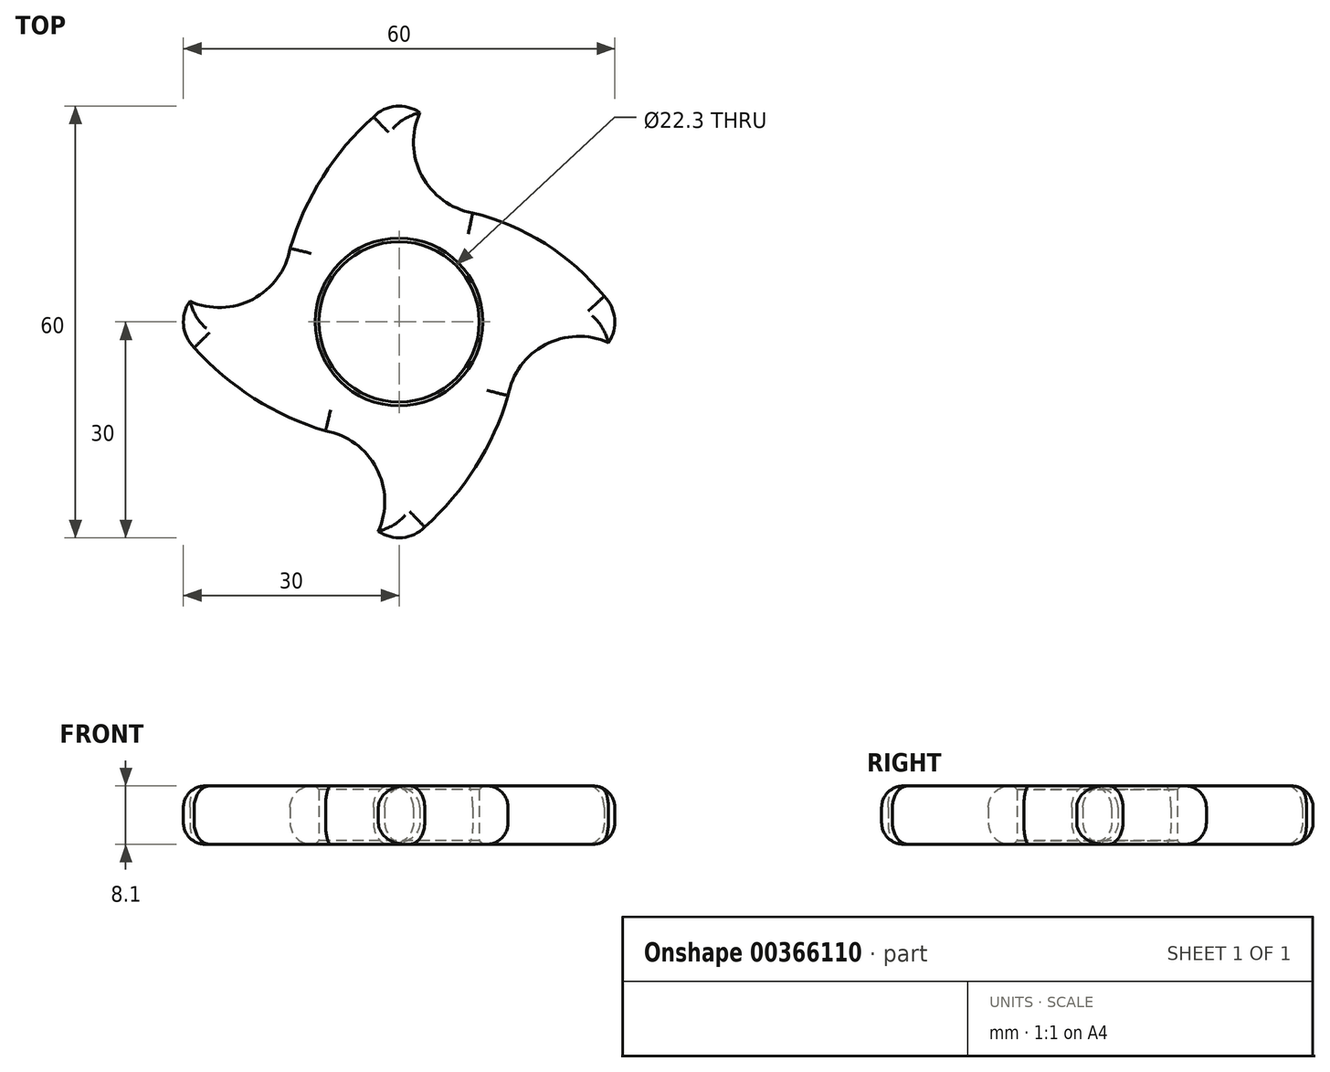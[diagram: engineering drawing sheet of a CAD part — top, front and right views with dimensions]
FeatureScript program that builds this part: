
annotation { "Feature Type Name" : "Feature", "Feature Type Description" : "" }
export const myFeature = defineFeature(function(context is Context, id is Id, definition is map)
    precondition{}
    {
        {
            var Q0;
            Q0=qCreatedBy(makeId("Top.planeOp"),FACE);
            var sketch = newSketch(context, id + "F0", { "sketchPlane" : qUnion([Q0])});
            skCircle(sketch, "E0", {"center": v(0, 0) * mm, "radius": 11.15 * mm});
            skArc(sketch, "E1", {"start": v(29.1, -2.88) * mm, "mid": v(29.98, 0.45) * mm, "end": v(28.51, 3.56) * mm});
            skArc(sketch, "E2", {"start": v(28.51, 3.56) * mm, "mid": v(20.33, 10.86) * mm, "end": v(10.23, 15.16) * mm});
            skArc(sketch, "E3.MirrorCS", {"start": v(-28.51, -3.56) * mm, "mid": v(-29.98, -0.45) * mm, "end": v(-29.1, 2.87) * mm});
            skArc(sketch, "E4.MirrorCS", {"start": v(-28.51, -3.56) * mm, "mid": v(-20.17, -10.62) * mm, "end": v(-10.23, -15.16) * mm});
            skArc(sketch, "E5", {"start": v(-29.1, 2.87) * mm, "mid": v(-20.33, 3.16) * mm, "end": v(-15.16, 10.23) * mm});
            skPoint(sketch, "E6.orphan", {"position": v(-28.51, 3.56) * mm});
            skPoint(sketch, "E7.visualSharp", {"position": v(-15.04, 12.9) * mm});
            skArc(sketch, "E8.MirrorCS", {"start": v(29.1, -2.87) * mm, "mid": v(20.33, -3.16) * mm, "end": v(15.16, -10.23) * mm});
            skPoint(sketch, "E9.orphan", {"position": v(28.51, -3.56) * mm});
            skArc(sketch, "E10.MirrorCS", {"start": v(-2.87, -29.1) * mm, "mid": v(-3.16, -20.33) * mm, "end": v(-10.23, -15.16) * mm});
            skArc(sketch, "E11.MirrorCS", {"start": v(3.56, -28.51) * mm, "mid": v(0.45, -29.98) * mm, "end": v(-2.88, -29.1) * mm});
            skArc(sketch, "E12.MirrorCS", {"start": v(3.56, -28.51) * mm, "mid": v(10.62, -20.17) * mm, "end": v(15.16, -10.23) * mm});
            skArc(sketch, "E13.MirrorCS", {"start": v(-3.56, 28.51) * mm, "mid": v(-10.62, 20.17) * mm, "end": v(-15.16, 10.23) * mm});
            skArc(sketch, "E14.MirrorCS", {"start": v(-3.56, 28.51) * mm, "mid": v(-0.45, 29.98) * mm, "end": v(2.88, 29.1) * mm});
            skArc(sketch, "E15.MirrorCS", {"start": v(2.87, 29.1) * mm, "mid": v(3.16, 20.33) * mm, "end": v(10.23, 15.16) * mm});
            skPoint(sketch, "E16.orphan", {"position": v(0, 16.05) * mm});
            skSolve(sketch);
        }
        {
            var Q0;
            Q0 = qSketchRegion(id + "F0", true);
            extrude(context, id + "F1", {"entities" : qUnion([Q0]), "depth" : 8.1 * mm});
        }
        {
            var Q0;
            Q0=makeQuery(id+"F1.opExtrude","CAP_EDGE",EDGE,{"disambiguationData":[OSD([sQuery(id+"F0.wireOp",EDGE,"E0")])],"isStart":false});
            var Q1;
            Q1=makeQuery(id+"F1.opExtrude","CAP_EDGE",EDGE,{"disambiguationData":[OSD([sQuery(id+"F0.wireOp",EDGE,"E0")])],"isStart":true});
            chamfer(context, id + "F2", {"entities" : qUnion([Q0, Q1]), "width" : .5 * mm, "tangentPropagation" : true});
        }
        {
            var Q0;
            Q0=makeQuery(id+"F1.opExtrude","CAP_EDGE",EDGE,{"disambiguationData":[OSD([sQuery(id+"F0.wireOp",EDGE,"E5")])],"isStart":false});
            var Q1;
            Q1=makeQuery(id+"F1.opExtrude","CAP_EDGE",EDGE,{"disambiguationData":[OSD([sQuery(id+"F0.wireOp",EDGE,"E13.MirrorCS")])],"isStart":false});
            var Q2;
            Q2=makeQuery(id+"F1.opExtrude","CAP_EDGE",EDGE,{"disambiguationData":[OSD([sQuery(id+"F0.wireOp",EDGE,"E14.MirrorCS")])],"isStart":false});
            var Q3;
            Q3=makeQuery(id+"F1.opExtrude","CAP_EDGE",EDGE,{"disambiguationData":[OSD([sQuery(id+"F0.wireOp",EDGE,"E15.MirrorCS")])],"isStart":false});
            var Q4;
            Q4=makeQuery(id+"F1.opExtrude","CAP_EDGE",EDGE,{"disambiguationData":[OSD([sQuery(id+"F0.wireOp",EDGE,"E2")])],"isStart":false});
            var Q5;
            Q5=makeQuery(id+"F1.opExtrude","CAP_EDGE",EDGE,{"disambiguationData":[OSD([sQuery(id+"F0.wireOp",EDGE,"E1")])],"isStart":false});
            var Q6;
            Q6=makeQuery(id+"F1.opExtrude","CAP_EDGE",EDGE,{"disambiguationData":[OSD([sQuery(id+"F0.wireOp",EDGE,"E8.MirrorCS")])],"isStart":false});
            var Q7;
            Q7=makeQuery(id+"F1.opExtrude","CAP_EDGE",EDGE,{"disambiguationData":[OSD([sQuery(id+"F0.wireOp",EDGE,"E12.MirrorCS")])],"isStart":false});
            var Q8;
            Q8=makeQuery(id+"F1.opExtrude","CAP_EDGE",EDGE,{"disambiguationData":[OSD([sQuery(id+"F0.wireOp",EDGE,"E11.MirrorCS")])],"isStart":false});
            var Q9;
            Q9=makeQuery(id+"F1.opExtrude","CAP_EDGE",EDGE,{"disambiguationData":[OSD([sQuery(id+"F0.wireOp",EDGE,"E10.MirrorCS")])],"isStart":false});
            var Q10;
            Q10=makeQuery(id+"F1.opExtrude","CAP_EDGE",EDGE,{"disambiguationData":[OSD([sQuery(id+"F0.wireOp",EDGE,"E4.MirrorCS")])],"isStart":false});
            var Q11;
            Q11=makeQuery(id+"F1.opExtrude","CAP_EDGE",EDGE,{"disambiguationData":[OSD([sQuery(id+"F0.wireOp",EDGE,"E3.MirrorCS")])],"isStart":false});
            fillet(context, id + "F3", {"entities" : qUnion([Q0, Q1, Q2, Q3, Q4, Q5, Q6, Q7, Q8, Q9, Q10, Q11]), "radius" : 3 * mm, "tangentPropagation" : true, "allowEdgeOverflow" : false});
        }
        {
            var Q0;
            Q0=makeQuery(id+"F1.opExtrude","CAP_EDGE",EDGE,{"disambiguationData":[OSD([sQuery(id+"F0.wireOp",EDGE,"E3.MirrorCS")])],"isStart":true});
            var Q1;
            Q1=makeQuery(id+"F1.opExtrude","CAP_EDGE",EDGE,{"disambiguationData":[OSD([sQuery(id+"F0.wireOp",EDGE,"E5")])],"isStart":true});
            var Q2;
            Q2=makeQuery(id+"F1.opExtrude","CAP_EDGE",EDGE,{"disambiguationData":[OSD([sQuery(id+"F0.wireOp",EDGE,"E13.MirrorCS")])],"isStart":true});
            var Q3;
            Q3=makeQuery(id+"F1.opExtrude","CAP_EDGE",EDGE,{"disambiguationData":[OSD([sQuery(id+"F0.wireOp",EDGE,"E14.MirrorCS")])],"isStart":true});
            var Q4;
            Q4=makeQuery(id+"F1.opExtrude","CAP_EDGE",EDGE,{"disambiguationData":[OSD([sQuery(id+"F0.wireOp",EDGE,"E15.MirrorCS")])],"isStart":true});
            var Q5;
            Q5=makeQuery(id+"F1.opExtrude","CAP_EDGE",EDGE,{"disambiguationData":[OSD([sQuery(id+"F0.wireOp",EDGE,"E2")])],"isStart":true});
            var Q6;
            Q6=makeQuery(id+"F1.opExtrude","CAP_EDGE",EDGE,{"disambiguationData":[OSD([sQuery(id+"F0.wireOp",EDGE,"E4.MirrorCS")])],"isStart":true});
            var Q7;
            Q7=makeQuery(id+"F1.opExtrude","CAP_EDGE",EDGE,{"disambiguationData":[OSD([sQuery(id+"F0.wireOp",EDGE,"E10.MirrorCS")])],"isStart":true});
            var Q8;
            Q8=makeQuery(id+"F1.opExtrude","CAP_EDGE",EDGE,{"disambiguationData":[OSD([sQuery(id+"F0.wireOp",EDGE,"E12.MirrorCS")])],"isStart":true});
            var Q9;
            Q9=makeQuery(id+"F1.opExtrude","CAP_EDGE",EDGE,{"disambiguationData":[OSD([sQuery(id+"F0.wireOp",EDGE,"E11.MirrorCS")])],"isStart":true});
            var Q10;
            Q10=makeQuery(id+"F1.opExtrude","CAP_EDGE",EDGE,{"disambiguationData":[OSD([sQuery(id+"F0.wireOp",EDGE,"E8.MirrorCS")])],"isStart":true});
            var Q11;
            Q11=makeQuery(id+"F1.opExtrude","CAP_EDGE",EDGE,{"disambiguationData":[OSD([sQuery(id+"F0.wireOp",EDGE,"E1")])],"isStart":true});
            fillet(context, id + "F4", {"entities" : qUnion([Q0, Q1, Q2, Q3, Q4, Q5, Q6, Q7, Q8, Q9, Q10, Q11]), "radius" : 3 * mm, "tangentPropagation" : true, "allowEdgeOverflow" : false});
        }
    });
